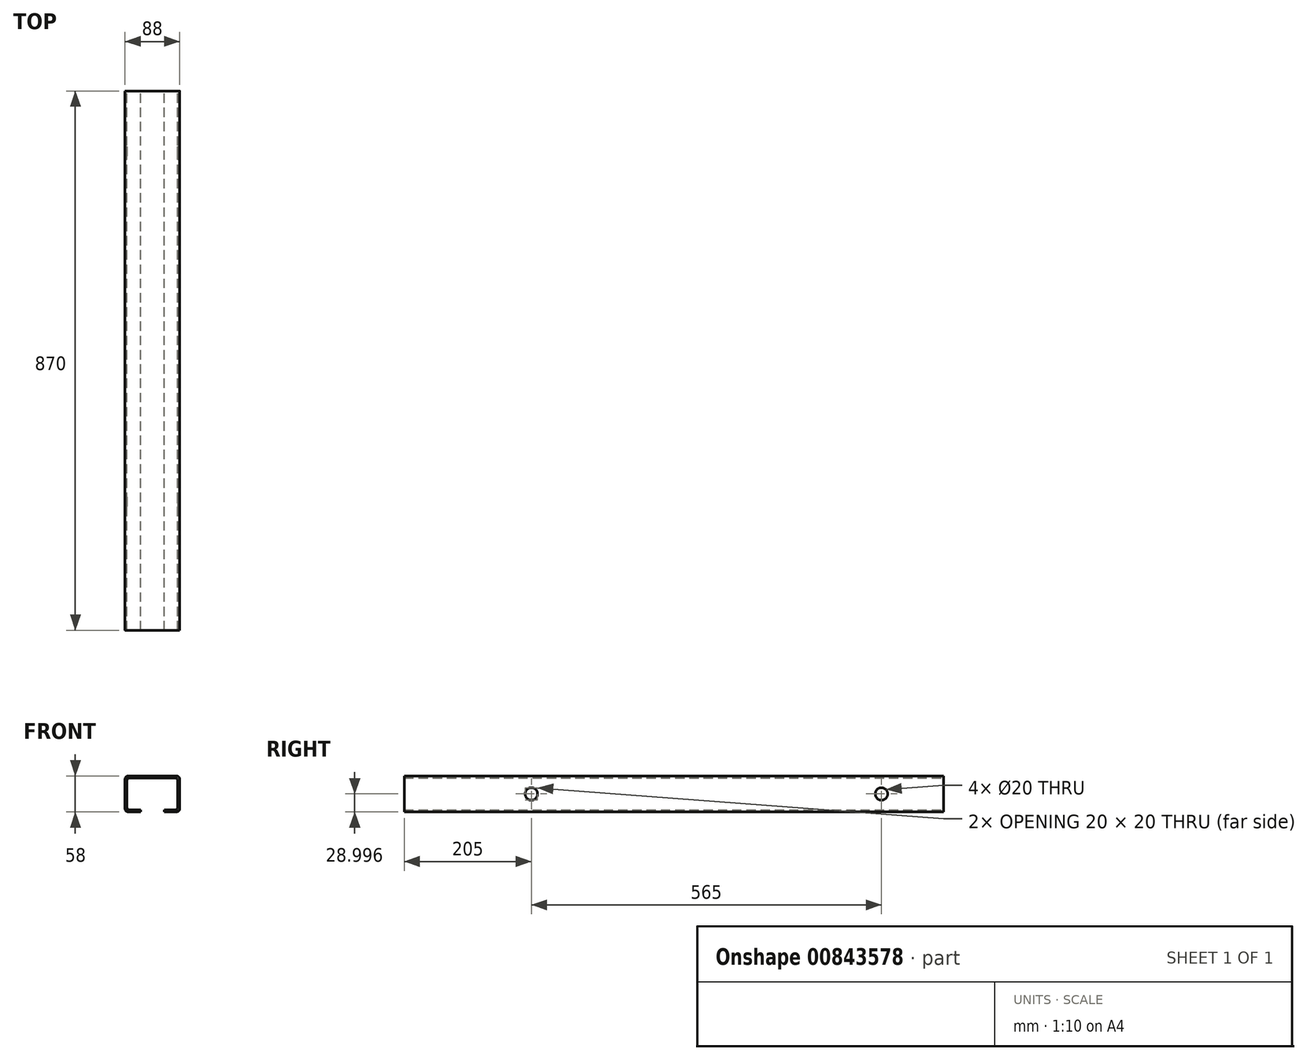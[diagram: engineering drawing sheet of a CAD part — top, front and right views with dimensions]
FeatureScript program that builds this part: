
annotation { "Feature Type Name" : "Feature", "Feature Type Description" : "" }
export const myFeature = defineFeature(function(context is Context, id is Id, definition is map)
    precondition{}
    {
        {
            var Q0;
            Q0=qCreatedBy(makeId("Front.planeOp"),FACE);
            var sketch = newSketch(context, id + "F0", { "sketchPlane" : qUnion([Q0])});
            skLineSegment(sketch, "E0", {"start": v(-12.75, -37.96) * mm, "end": v(-37.75, -37.96) * mm});
            skLineSegment(sketch, "E1", {"start": v(-37.75, -37.96) * mm, "end": v(-37.75, 20.04) * mm});
            skLineSegment(sketch, "E2", {"start": v(-37.75, 20.04) * mm, "end": v(50.25, 20.04) * mm});
            skLineSegment(sketch, "E3", {"start": v(50.25, 20.04) * mm, "end": v(50.25, -37.96) * mm});
            skLineSegment(sketch, "E4", {"start": v(50.25, -37.96) * mm, "end": v(25.25, -37.96) * mm});
            skLineSegment(sketch, "E5", {"start": v(25.25, -37.96) * mm, "end": v(25.25, -34.96) * mm});
            skLineSegment(sketch, "E6", {"start": v(25.25, -34.96) * mm, "end": v(47.25, -34.96) * mm});
            skLineSegment(sketch, "E7", {"start": v(47.25, -34.96) * mm, "end": v(47.25, 17.04) * mm});
            skLineSegment(sketch, "E8", {"start": v(47.25, 17.04) * mm, "end": v(-34.75, 17.04) * mm});
            skLineSegment(sketch, "E9", {"start": v(-34.75, 17.04) * mm, "end": v(-34.75, -34.96) * mm});
            skLineSegment(sketch, "E10", {"start": v(-34.75, -34.96) * mm, "end": v(-12.75, -34.96) * mm});
            skLineSegment(sketch, "E11", {"start": v(-12.75, -34.96) * mm, "end": v(-12.75, -37.96) * mm});
            skSolve(sketch);
        }
        {
            var Q0;
            Q0 = qSketchRegion(id + "F0", true);
            extrude(context, id + "F1", {"entities" : qUnion([Q0]), "depth" : 870 * mm, "offsetDistance" : 25 * mm});
        }
        {
            var Q0;
            Q0=makeQuery(id+"F1.opExtrude","SWEPT_EDGE",EDGE,{"disambiguationData":[OSD([sQuery(id+"F0.wireOp",EDGE,"E1"),sQuery(id+"F0.wireOp",EDGE,"E2")])]});
            var Q1;
            Q1=makeQuery(id+"F1.opExtrude","SWEPT_EDGE",EDGE,{"disambiguationData":[OSD([sQuery(id+"F0.wireOp",EDGE,"E2"),sQuery(id+"F0.wireOp",EDGE,"E3")])]});
            var Q2;
            Q2=makeQuery(id+"F1.opExtrude","SWEPT_EDGE",EDGE,{"disambiguationData":[OSD([sQuery(id+"F0.wireOp",EDGE,"E0"),sQuery(id+"F0.wireOp",EDGE,"E1")])]});
            var Q3;
            Q3=makeQuery(id+"F1.opExtrude","SWEPT_EDGE",EDGE,{"disambiguationData":[OSD([sQuery(id+"F0.wireOp",EDGE,"E3"),sQuery(id+"F0.wireOp",EDGE,"E4")])]});
            fillet(context, id + "F2", {"entities" : qUnion([Q0, Q1, Q2, Q3]), "radius" : 5 * mm, "tangentPropagation" : true, "allowEdgeOverflow" : false});
        }
        {
            var Q0;
            Q0=makeQuery(id+"F1.opExtrude","SWEPT_EDGE",EDGE,{"disambiguationData":[OSD([sQuery(id+"F0.wireOp",EDGE,"E6"),sQuery(id+"F0.wireOp",EDGE,"E7")])]});
            var Q1;
            Q1=makeQuery(id+"F1.opExtrude","SWEPT_EDGE",EDGE,{"disambiguationData":[OSD([sQuery(id+"F0.wireOp",EDGE,"E7"),sQuery(id+"F0.wireOp",EDGE,"E8")])]});
            var Q2;
            Q2=makeQuery(id+"F1.opExtrude","SWEPT_EDGE",EDGE,{"disambiguationData":[OSD([sQuery(id+"F0.wireOp",EDGE,"E9"),sQuery(id+"F0.wireOp",EDGE,"E10")])]});
            var Q3;
            Q3=makeQuery(id+"F1.opExtrude","SWEPT_EDGE",EDGE,{"disambiguationData":[OSD([sQuery(id+"F0.wireOp",EDGE,"E8"),sQuery(id+"F0.wireOp",EDGE,"E9")])]});
            fillet(context, id + "F3", {"entities" : qUnion([Q0, Q1, Q2, Q3]), "radius" : 5 * mm, "tangentPropagation" : true, "allowEdgeOverflow" : false});
        }
        {
            var Q0;
            Q0=makeQuery(id+"F1.opExtrude","SWEPT_FACE",FACE,{"disambiguationData":[OSD([sQuery(id+"F0.wireOp",EDGE,"E3")])]});
            var sketch = newSketch(context, id + "F4", { "sketchPlane" : qUnion([Q0])});
            skCircle(sketch, "E12", {"center": v(-665, -8.96) * mm, "radius": 10 * mm});
            skCircle(sketch, "E13", {"center": v(-100, -8.96) * mm, "radius": 10 * mm});
            skSolve(sketch);
        }
        {
            var Q0;
            Q0 = qSketchRegion(id + "F4", true);
            extrude(context, id + "F5", {"entities" : qUnion([Q0]), "operationType" : NewBodyOperationType.REMOVE, "endBound" : BoundingType.THROUGH_ALL, "oppositeDirection" : true, "depth" : 25 * mm, "offsetDistance" : 25 * mm});
        }
    });
